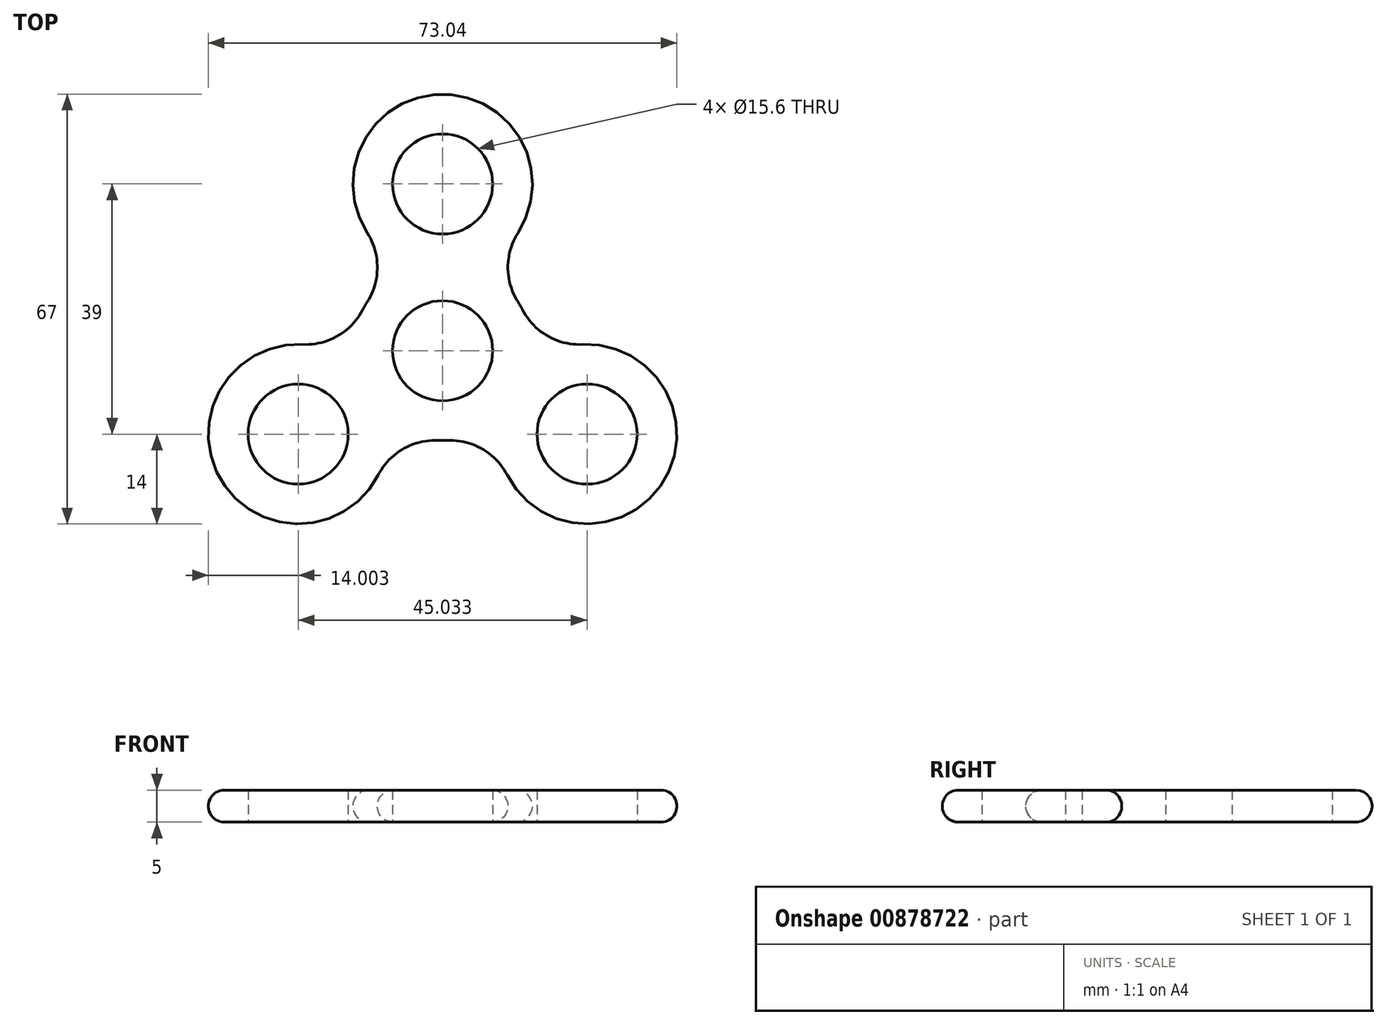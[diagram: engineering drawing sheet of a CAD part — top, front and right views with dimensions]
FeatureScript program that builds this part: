
annotation { "Feature Type Name" : "Feature", "Feature Type Description" : "" }
export const myFeature = defineFeature(function(context is Context, id is Id, definition is map)
    precondition{}
    {
        {
            var Q0;
            Q0=qCreatedBy(makeId("Top.planeOp"),FACE);
            var sketch = newSketch(context, id + "F0", { "sketchPlane" : qUnion([Q0])});
            skCircle(sketch, "E0", {"center": v(0, 0) * mm, "radius": 7.8 * mm});
            skCircle(sketch, "E1", {"center": v(0, 26) * mm, "radius": 7.8 * mm});
            skCircle(sketch, "E2", {"center": v(22.52, -13) * mm, "radius": 7.8 * mm});
            skCircle(sketch, "E3", {"center": v(-22.52, -13) * mm, "radius": 7.8 * mm});
            skArc(sketch, "E4", {"start": v(-13.86, -2) * mm, "mid": v(-34.64, -20) * mm, "end": v(-8.66, -11) * mm});
            skArc(sketch, "E5", {"start": v(8.66, -11) * mm, "mid": v(34.64, -20) * mm, "end": v(13.86, -2) * mm});
            skArc(sketch, "E6", {"start": v(5.2, 13) * mm, "mid": v(0, 40) * mm, "end": v(-5.2, 13) * mm});
            skArc(sketch, "E7", {"start": v(-5.2, 13) * mm, "mid": v(-12.12, 7) * mm, "end": v(-13.86, -2) * mm});
            skArc(sketch, "E8.trimOffspring", {"start": v(-8.66, -11) * mm, "mid": v(0, -14) * mm, "end": v(8.66, -11) * mm});
            skArc(sketch, "E9.trimOffspring", {"start": v(13.86, -2) * mm, "mid": v(12.12, 7) * mm, "end": v(5.2, 13) * mm});
            skSolve(sketch);
        }
        {
            var Q0;
            Q0=makeQuery(id+"F0.imprint","IMPRINT",FACE,{"disambiguationData":[TD([[makeQuery(id+"F0.imprint","IMPRINT",EDGE,{"derivedFrom":sQuery(id+"F0.wireOp",EDGE,"E0")}),-1.0]])]});
            extrude(context, id + "F1", {"entities" : qUnion([Q0]), "depth" : 5 * mm, "offsetDistance" : 25 * mm});
        }
        {
            var Q0;
            Q0=makeQuery(id+"F1.opExtrude","SWEPT_EDGE",EDGE,{"disambiguationData":[OSD([sQuery(id+"F0.wireOp",EDGE,"E4"),sQuery(id+"F0.wireOp",EDGE,"E8.trimOffspring")])]});
            var Q1;
            Q1=makeQuery(id+"F1.opExtrude","SWEPT_EDGE",EDGE,{"disambiguationData":[OSD([sQuery(id+"F0.wireOp",EDGE,"E5"),sQuery(id+"F0.wireOp",EDGE,"E8.trimOffspring")])]});
            var Q2;
            Q2=makeQuery(id+"F1.opExtrude","SWEPT_EDGE",EDGE,{"disambiguationData":[OSD([sQuery(id+"F0.wireOp",EDGE,"E5"),sQuery(id+"F0.wireOp",EDGE,"E9.trimOffspring")])]});
            var Q3;
            Q3=makeQuery(id+"F1.opExtrude","SWEPT_EDGE",EDGE,{"disambiguationData":[OSD([sQuery(id+"F0.wireOp",EDGE,"E6"),sQuery(id+"F0.wireOp",EDGE,"E9.trimOffspring")])]});
            var Q4;
            Q4=makeQuery(id+"F1.opExtrude","SWEPT_EDGE",EDGE,{"disambiguationData":[OSD([sQuery(id+"F0.wireOp",EDGE,"E6"),sQuery(id+"F0.wireOp",EDGE,"E7")])]});
            var Q5;
            Q5=makeQuery(id+"F1.opExtrude","SWEPT_EDGE",EDGE,{"disambiguationData":[OSD([sQuery(id+"F0.wireOp",EDGE,"E4"),sQuery(id+"F0.wireOp",EDGE,"E7")])]});
            fillet(context, id + "F2", {"entities" : qUnion([Q0, Q1, Q2, Q3, Q4, Q5]), "radius" : 10 * mm, "tangentPropagation" : true, "allowEdgeOverflow" : false});
        }
        {
            var Q0;
            Q0=makeQuery(id+"F1.opExtrude","CAP_EDGE",EDGE,{"disambiguationData":[OSD([sQuery(id+"F0.wireOp",EDGE,"E6")])],"isStart":false});
            var Q1;
            {var subQ0=sQuery(id+"F0.wireOp",EDGE,"E7");var subQ1=sQuery(id+"F0.wireOp",EDGE,"E4");Q1=makeQuery(id+"F2.opFillet","BLEND_EDGE",EDGE,{"blendedFrom":[makeQuery(id+"F1.opExtrude","SWEPT_EDGE",EDGE,{"disambiguationData":[OSD([subQ1,subQ0])]}),makeQuery(id+"F1.opExtrude","CAP_FACE",FACE,{"disambiguationData":[OSD([sQuery(id+"F0.wireOp",EDGE,"E0"),sQuery(id+"F0.wireOp",EDGE,"E1"),sQuery(id+"F0.wireOp",EDGE,"E2"),sQuery(id+"F0.wireOp",EDGE,"E3"),subQ1,sQuery(id+"F0.wireOp",EDGE,"E5"),sQuery(id+"F0.wireOp",EDGE,"E6"),subQ0,sQuery(id+"F0.wireOp",EDGE,"E8.trimOffspring"),sQuery(id+"F0.wireOp",EDGE,"E9.trimOffspring")])],"isStart":true})],"blendedInto":[makeQuery(id+"F1.opExtrude","CAP_FACE",FACE,{"disambiguationData":[OSD([sQuery(id+"F0.wireOp",EDGE,"E0"),sQuery(id+"F0.wireOp",EDGE,"E1"),sQuery(id+"F0.wireOp",EDGE,"E2"),sQuery(id+"F0.wireOp",EDGE,"E3"),subQ1,sQuery(id+"F0.wireOp",EDGE,"E5"),sQuery(id+"F0.wireOp",EDGE,"E6"),subQ0,sQuery(id+"F0.wireOp",EDGE,"E8.trimOffspring"),sQuery(id+"F0.wireOp",EDGE,"E9.trimOffspring")])],"isStart":true})]});}
            fillet(context, id + "F3", {"entities" : qUnion([Q0, Q1]), "radius" : 2.5 * mm, "tangentPropagation" : true, "allowEdgeOverflow" : false});
        }
    });
